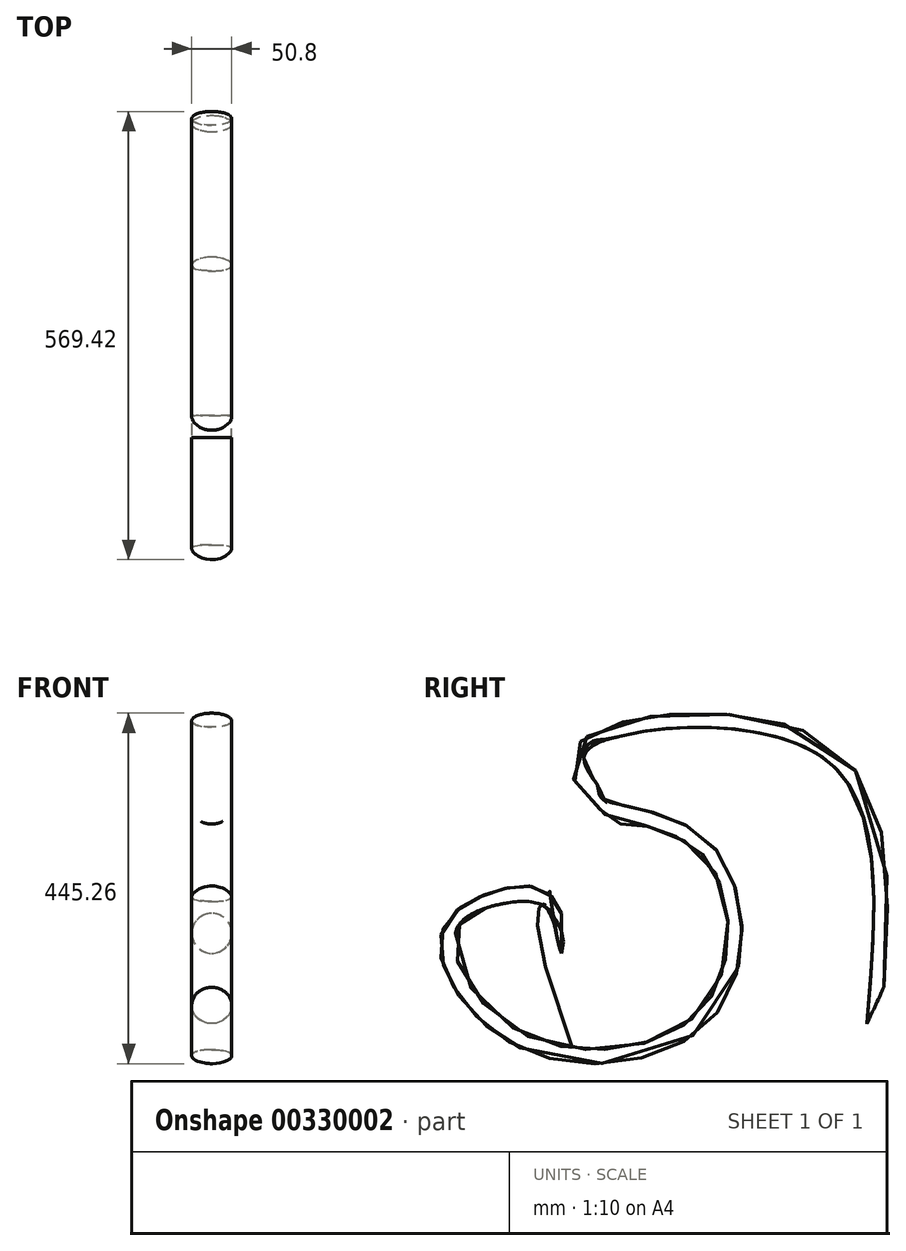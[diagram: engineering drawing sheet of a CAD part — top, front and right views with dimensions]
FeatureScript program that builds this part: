
annotation { "Feature Type Name" : "Feature", "Feature Type Description" : "" }
export const myFeature = defineFeature(function(context is Context, id is Id, definition is map)
    precondition{}
    {
        {
            var Q0;
            Q0=qCreatedBy(makeId("Front.planeOp"),FACE);
            var sketch = newSketch(context, id + "F0", { "sketchPlane" : qUnion([Q0])});
            skCircle(sketch, "E0", {"center": v(0, 0) * mm, "radius": 25.4 * mm});
            skSolve(sketch);
        }
        {
            var Q0;
            Q0=qCreatedBy(makeId("Right.planeOp"),FACE);
            var sketch = newSketch(context, id + "F1", { "sketchPlane" : qUnion([Q0])});
            skFitSpline(sketch, "E1", {"points": [v(0, 0) * mm, v(-24.24, 39.53) * mm, v(-84.48, 41.89) * mm, v(-140.49, -8) * mm, v(-45.6, -137.18) * mm, v(188.24, -95.34) * mm, v(184.5, 103.39) * mm, v(72.44, 154.94) * mm, v(51.52, 169.88) * mm, v(29.1, 229.65) * mm, v(324.21, 237.12) * mm, v(398.92, -91.6) * mm], "startDerivative": vector(-323.05, 862.49) * mm, "endDerivative": vector(-208.54, -2781.9) * mm});
            skSolve(sketch);
        }
        {
            var Q0;
            Q0=makeQuery(id+"F0.imprint","IMPRINT",FACE,{"disambiguationData":[TD([[makeQuery(id+"F0.imprint","IMPRINT",EDGE,{"derivedFrom":sQuery(id+"F0.wireOp",EDGE,"E0")}),1.0]])]});
            var Q1;
            Q1=sQuery(id+"F1.wireOp",EDGE,"E1");
            sweep(context, id + "F2", {"profiles" : qUnion([Q0]), "path" : qUnion([Q1])});
        }
        {
            var Q0;
            Q0=makeQuery(id+"F2.opSweep","CAP_FACE",FACE,{"disambiguationData":[OSD([sQuery(id+"F0.wireOp",EDGE,"E0"),sQuery(id+"F1.wireOp",VERTEX,"E1.end")])],"isStart":false});
            shell(context, id + "F3", {"entities" : qUnion([Q0]), "thickness" : 0.03 * mm});
        }
    });
